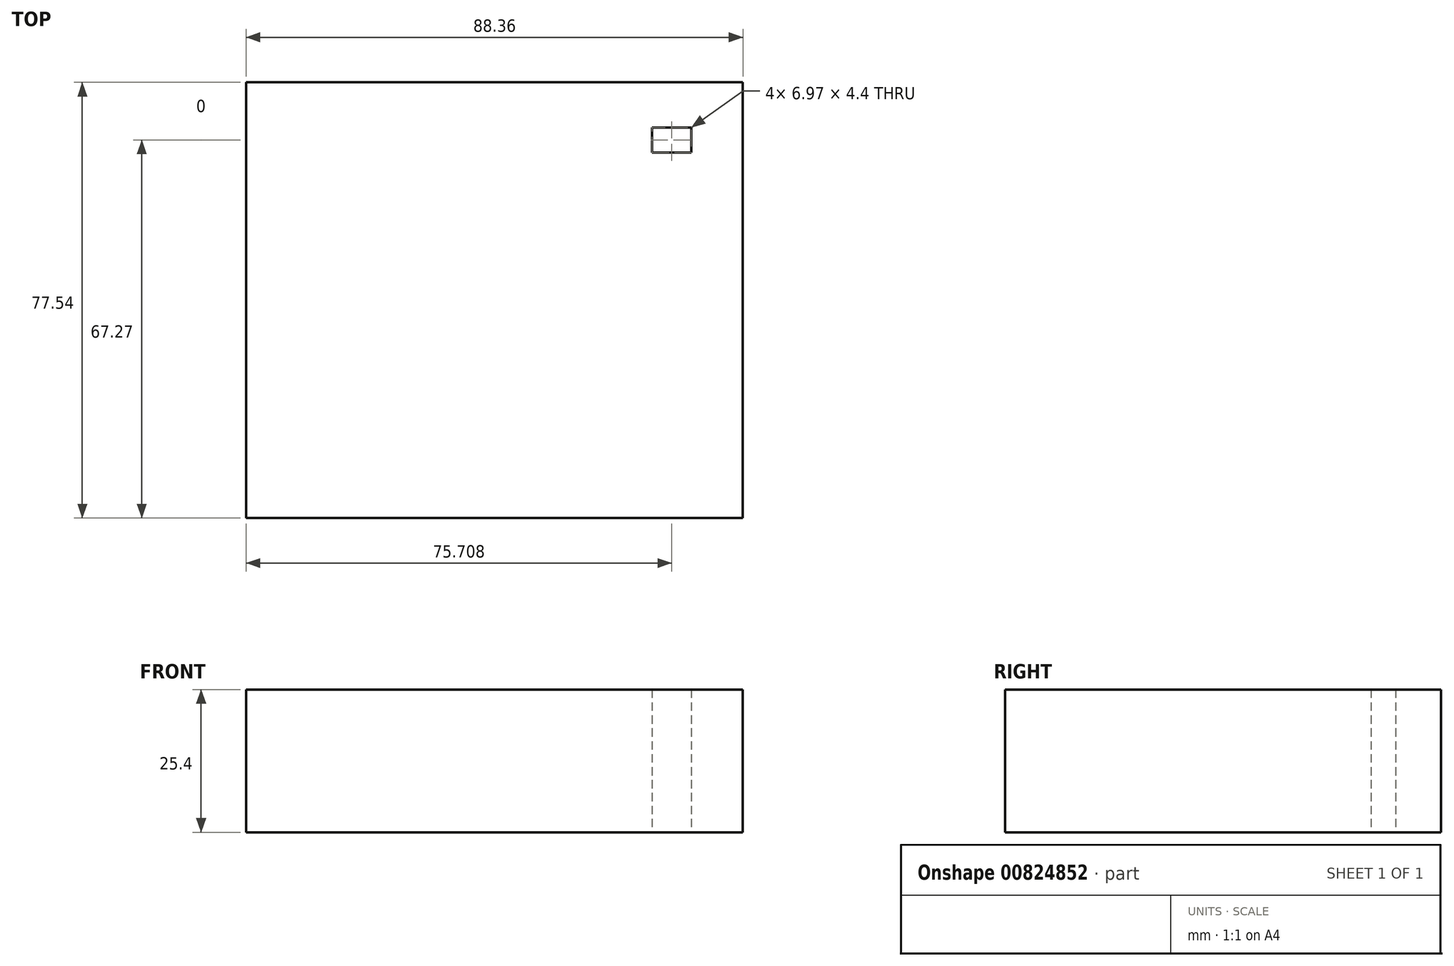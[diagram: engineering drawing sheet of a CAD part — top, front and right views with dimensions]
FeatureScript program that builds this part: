
annotation { "Feature Type Name" : "Feature", "Feature Type Description" : "" }
export const myFeature = defineFeature(function(context is Context, id is Id, definition is map)
    precondition{}
    {
        {
            var Q0;
            Q0=qCreatedBy(makeId("Top.planeOp"),FACE);
            var sketch = newSketch(context, id + "F0", { "sketchPlane" : qUnion([Q0])});
            skLineSegment(sketch, "E0.bottom", {"start": v(45.46, 48.76) * mm, "end": v(38.5, 48.76) * mm});
            skLineSegment(sketch, "E0.top", {"start": v(45.46, 53.16) * mm, "end": v(38.5, 53.16) * mm});
            skLineSegment(sketch, "E0.left", {"start": v(45.46, 48.76) * mm, "end": v(45.46, 53.16) * mm});
            skLineSegment(sketch, "E0.right", {"start": v(38.5, 48.76) * mm, "end": v(38.5, 53.16) * mm});
            skLineSegment(sketch, "E1.bottom", {"start": v(-33.73, -16.31) * mm, "end": v(54.63, -16.31) * mm});
            skLineSegment(sketch, "E1.top", {"start": v(-33.73, 61.23) * mm, "end": v(54.63, 61.23) * mm});
            skLineSegment(sketch, "E1.left", {"start": v(-33.73, -16.31) * mm, "end": v(-33.73, 61.23) * mm});
            skLineSegment(sketch, "E1.right", {"start": v(54.63, -16.31) * mm, "end": v(54.63, 61.23) * mm});
            skSolve(sketch);
        }
        {
            var Q0;
            Q0=makeQuery(id+"F0.imprint","IMPRINT",FACE,{"disambiguationData":[TD([[makeQuery(id+"F0.imprint","IMPRINT",EDGE,{"derivedFrom":sQuery(id+"F0.wireOp",EDGE,"E0.bottom")}),1.0]])]});
            extrude(context, id + "F1", {"entities" : qUnion([Q0]), "depth" : 25.4 * mm, "offsetDistance" : 25.4 * mm});
        }
    });
